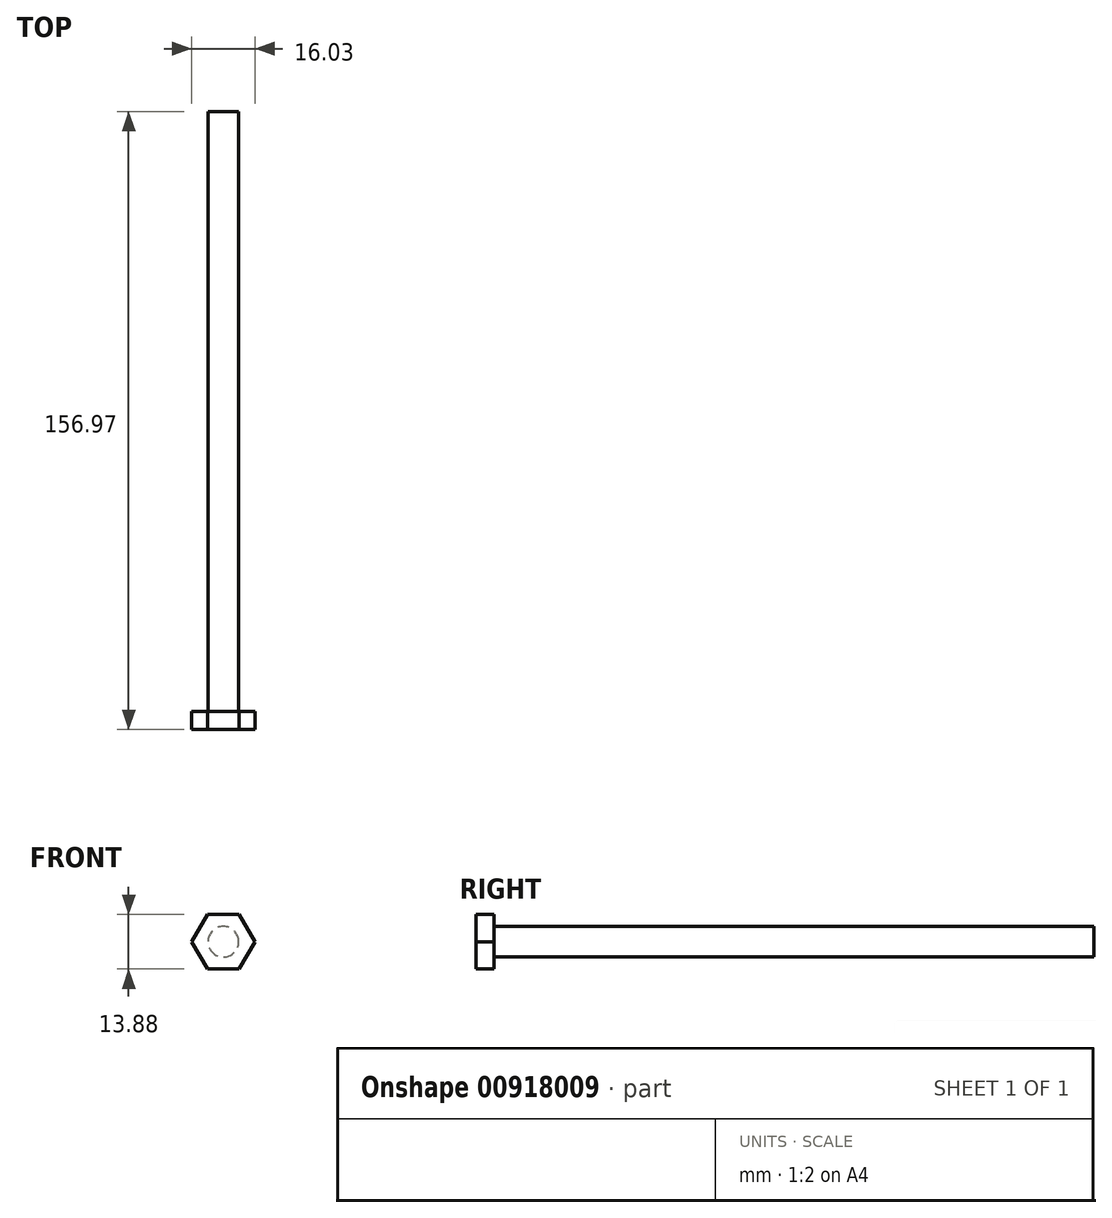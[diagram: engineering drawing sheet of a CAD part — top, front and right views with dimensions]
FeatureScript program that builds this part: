
annotation { "Feature Type Name" : "Feature", "Feature Type Description" : "" }
export const myFeature = defineFeature(function(context is Context, id is Id, definition is map)
    precondition{}
    {
        {
            var Q0;
            Q0=qCreatedBy(makeId("Front.planeOp"),FACE);
            var sketch = newSketch(context, id + "F0", { "sketchPlane" : qUnion([Q0])});
            skCircle(sketch, "E0", {"center": v(-66.59, 45.85) * mm, "radius": 3.9 * mm});
            skSolve(sketch);
        }
        {
            var Q0;
            Q0 = qSketchRegion(id + "F0", true);
            extrude(context, id + "F1", {"entities" : qUnion([Q0]), "depth" : 152.4 * mm, "offsetDistance" : 25.4 * mm});
        }
        {
            var Q0;
            Q0=makeQuery(id+"F1.opExtrude","CAP_FACE",FACE,{"disambiguationData":[OSD([sQuery(id+"F0.wireOp",EDGE,"E0")])],"isStart":false});
            var sketch = newSketch(context, id + "F2", { "sketchPlane" : qUnion([Q0])});
            skCircle(sketch, "E1.cCircle", {"center": v(-66.59, 45.85) * mm, "radius": 6.94 * mm, "construction": true});
            skLineSegment(sketch, "E1.0", {"start": v(-62.58, 38.9) * mm, "end": v(-70.6, 38.9) * mm});
            skLineSegment(sketch, "E1.1", {"start": v(-70.6, 38.9) * mm, "end": v(-74.6, 45.85) * mm});
            skLineSegment(sketch, "E1.2", {"start": v(-74.6, 45.85) * mm, "end": v(-70.6, 52.79) * mm});
            skLineSegment(sketch, "E1.3", {"start": v(-70.6, 52.79) * mm, "end": v(-62.58, 52.79) * mm});
            skLineSegment(sketch, "E1.4", {"start": v(-62.58, 52.79) * mm, "end": v(-58.57, 45.85) * mm});
            skLineSegment(sketch, "E1.5", {"start": v(-58.57, 45.85) * mm, "end": v(-62.58, 38.9) * mm});
            skPoint(sketch, "E1.0.midPoint", {"position": v(-66.59, 38.9) * mm});
            skSolve(sketch);
        }
        {
            var Q0;
            Q0=makeQuery(id+"F1.opExtrude","SWEPT_BODY",BODY,{"disambiguationData":[OSD([sQuery(id+"F0.wireOp",EDGE,"E0")])]});
            transform(context, id + "F3", {"entities" : qUnion([Q0]), "transformType" : TransformType.TRANSLATION_3D, "dx" : -51.05 * mm, "dy" : 57.15 * mm, "dz" : -154.94 * mm, "makeCopy" : true});
        }
        {
            var Q0;
            Q0=makeQuery(id+"F3.opPattern","COPY",BODY,{"derivedFrom":makeQuery(id+"F1.opExtrude","SWEPT_BODY",BODY,{"disambiguationData":[OSD([sQuery(id+"F0.wireOp",EDGE,"E0")])]}),"instanceName":"1"});
            deleteBodies(context, id + "F4", {"entities" : qUnion([Q0])});
        }
        {
            var Q0;
            Q0 = qSketchRegion(id + "F2", true);
            extrude(context, id + "F5", {"entities" : qUnion([Q0]), "operationType" : NewBodyOperationType.ADD, "depth" : 4.57 * mm, "offsetDistance" : 25.4 * mm});
        }
    });
